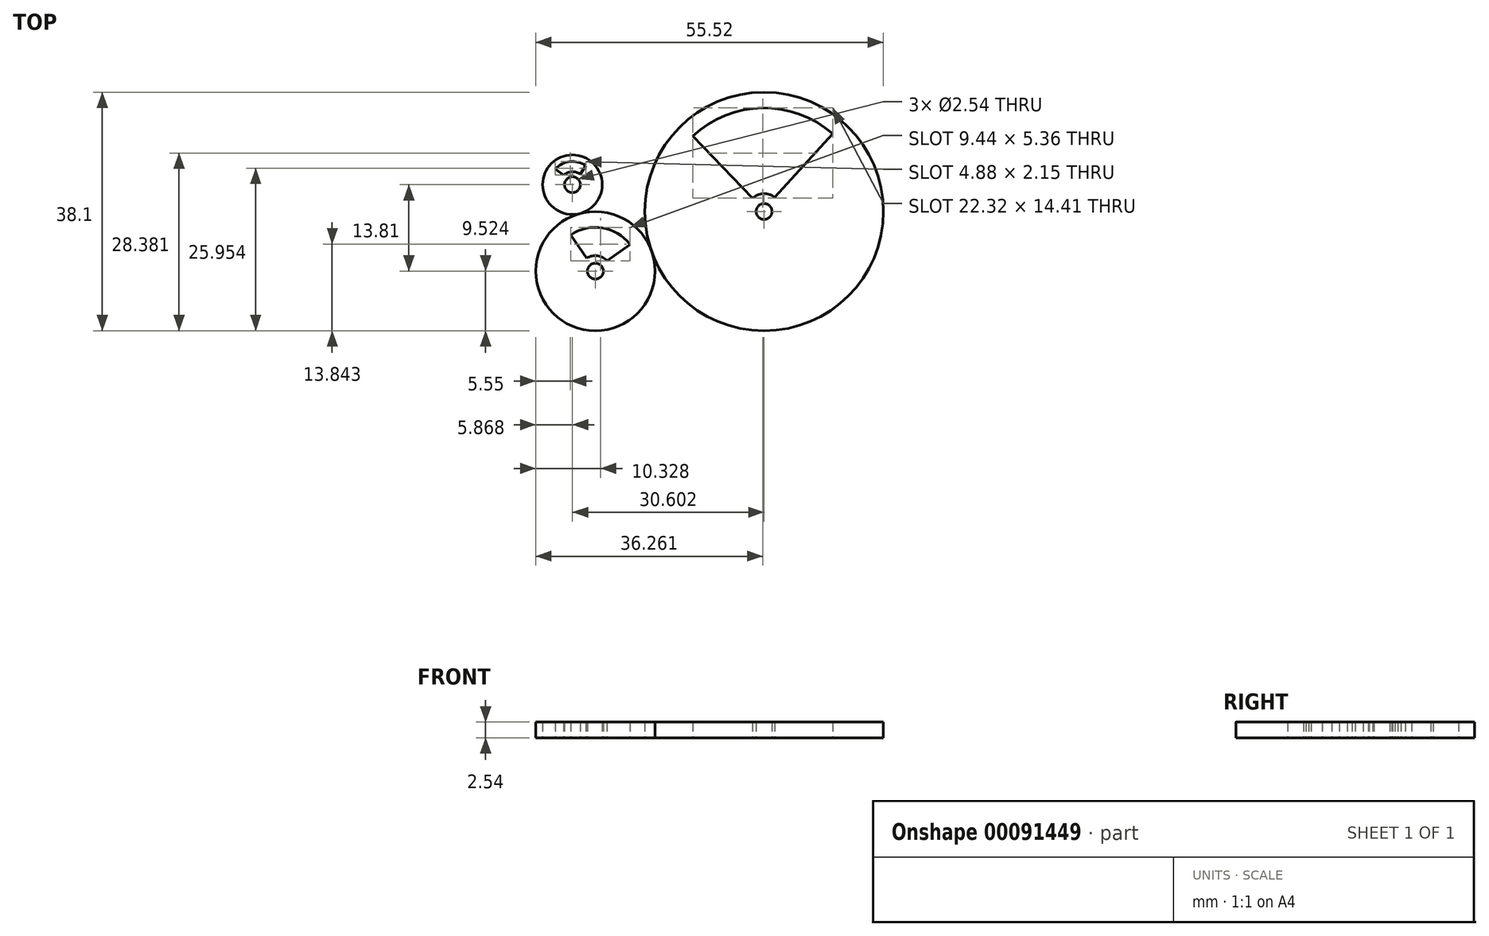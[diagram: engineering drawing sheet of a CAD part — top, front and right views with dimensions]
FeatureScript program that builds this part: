
annotation { "Feature Type Name" : "Feature", "Feature Type Description" : "" }
export const myFeature = defineFeature(function(context is Context, id is Id, definition is map)
    precondition{}
    {
        {
            var Q0;
            Q0=qCreatedBy(makeId("Top.planeOp"),FACE);
            var sketch = newSketch(context, id + "F0", { "sketchPlane" : qUnion([Q0])});
            skCircle(sketch, "E0", {"center": v(-21.65, -6.25) * mm, "radius": 9.53 * mm});
            skCircle(sketch, "E1", {"center": v(-25.31, 7.56) * mm, "radius": 4.76 * mm});
            skCircle(sketch, "E2", {"center": v(5.29, 3.28) * mm, "radius": 19.05 * mm});
            skCircle(sketch, "E3", {"center": v(-21.65, -6.25) * mm, "radius": 1.27 * mm});
            skCircle(sketch, "E4", {"center": v(-25.31, 7.56) * mm, "radius": 1.27 * mm});
            skCircle(sketch, "E5", {"center": v(5.29, 3.28) * mm, "radius": 1.27 * mm});
            skLineSegment(sketch, "E6", {"start": v(-28.07, 10.06) * mm, "end": v(-26.7, 9.11) * mm});
            skLineSegment(sketch, "E7", {"start": v(-23.2, 10.62) * mm, "end": v(-24.08, 9.24) * mm});
            skLineSegment(sketch, "E8", {"start": v(-25.57, -0.47) * mm, "end": v(-23.02, -4.17) * mm});
            skLineSegment(sketch, "E9", {"start": v(-19.78, -4.6) * mm, "end": v(-16.13, -1.98) * mm});
            skArc(sketch, "E10", {"start": v(-16.13, -1.98) * mm, "mid": v(-20.55, 0.67) * mm, "end": v(-25.57, -0.47) * mm});
            skArc(sketch, "E11", {"start": v(-19.78, -4.6) * mm, "mid": v(-21.32, -3.78) * mm, "end": v(-23.02, -4.17) * mm});
            skArc(sketch, "E12", {"start": v(-23.2, 10.62) * mm, "mid": v(-25.73, 11.24) * mm, "end": v(-28.07, 10.06) * mm});
            skArc(sketch, "E13", {"start": v(-24.08, 9.24) * mm, "mid": v(-25.41, 9.63) * mm, "end": v(-26.7, 9.11) * mm});
            skLineSegment(sketch, "E14", {"start": v(-6.08, 15.33) * mm, "end": v(3.4, 5.4) * mm});
            skLineSegment(sketch, "E15", {"start": v(16.24, 15.7) * mm, "end": v(7.01, 5.54) * mm});
            skArc(sketch, "E16", {"start": v(7.01, 5.54) * mm, "mid": v(5.19, 6.11) * mm, "end": v(3.4, 5.4) * mm});
            skArc(sketch, "E17", {"start": v(16.24, 15.7) * mm, "mid": v(5, 19.82) * mm, "end": v(-6.08, 15.33) * mm});
            skSolve(sketch);
        }
        {
            var Q0;
            Q0=makeQuery(id+"F0.imprint","IMPRINT",FACE,{"disambiguationData":[TD([[makeQuery(id+"F0.imprint","IMPRINT",EDGE,{"derivedFrom":sQuery(id+"F0.wireOp",EDGE,"E1")}),1.0]])]});
            var Q1;
            {var subQ0=sQuery(id+"F0.wireOp",EDGE,"E0");var subQ1=makeQuery(id+"F0.imprint","INTERSECT",VERTEX,{"derivedFrom":[subQ0,sQuery(id+"F0.wireOp",EDGE,"E1")]});Q1=makeQuery(id+"F0.imprint","IMPRINT",FACE,{"disambiguationData":[TD([[makeQuery(id+"F0.imprint","IMPRINT",EDGE,{"disambiguationData":[TD([[subQ1,1.0]])],"derivedFrom":subQ0}),1.0]])]});}
            var Q2;
            Q2=makeQuery(id+"F0.imprint","IMPRINT",FACE,{"disambiguationData":[TD([[makeQuery(id+"F0.imprint","IMPRINT",EDGE,{"derivedFrom":sQuery(id+"F0.wireOp",EDGE,"E2")}),1.0]])]});
            extrude(context, id + "F1", {"entities" : qUnion([Q0, Q1, Q2]), "depth" : 2.54 * mm});
        }
    });
